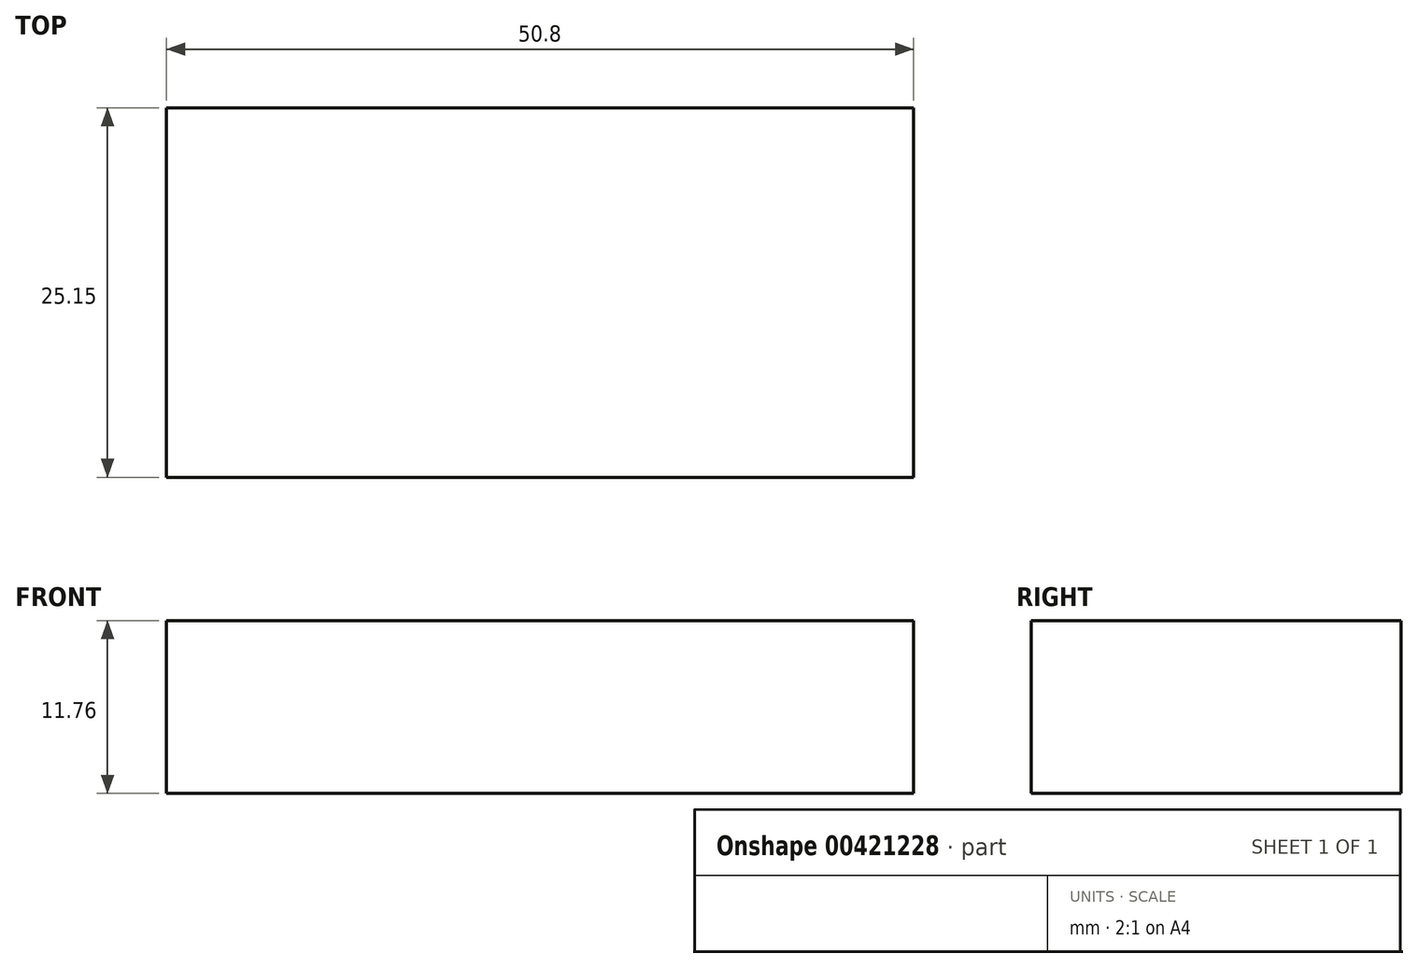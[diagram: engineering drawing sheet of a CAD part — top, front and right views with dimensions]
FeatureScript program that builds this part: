
annotation { "Feature Type Name" : "Feature", "Feature Type Description" : "" }
export const myFeature = defineFeature(function(context is Context, id is Id, definition is map)
    precondition{}
    {
        {
            var Q0;
            Q0=qCreatedBy(makeId("Top.planeOp"),FACE);
            var sketch = newSketch(context, id + "F0", { "sketchPlane" : qUnion([Q0])});
            skLineSegment(sketch, "E0.bottom", {"start": v(0, 0) * mm, "end": v(50.8, 0) * mm});
            skLineSegment(sketch, "E0.top", {"start": v(0, 25.15) * mm, "end": v(50.8, 25.15) * mm});
            skLineSegment(sketch, "E0.left", {"start": v(0, 0) * mm, "end": v(0, 25.15) * mm});
            skLineSegment(sketch, "E0.right", {"start": v(50.8, 0) * mm, "end": v(50.8, 25.15) * mm});
            skSolve(sketch);
        }
        {
            var Q0;
            Q0 = qSketchRegion(id + "F0", true);
            extrude(context, id + "F1", {"entities" : qUnion([Q0]), "depth" : 11.76 * mm});
        }
    });
